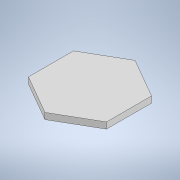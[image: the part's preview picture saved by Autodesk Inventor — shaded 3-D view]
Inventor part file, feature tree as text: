
AUTODESK INVENTOR PART (.ipt)
format: ipt  version: 2022.3 (Build 263350000, 350)  size: 94,208 bytes
history: native  units: in
note: dims shown in document units (in); Inventor stores cm internally (conversion verified against a paired STEP export)
features: extrude x1, sketch x1
ambient origin geometry x8: Origin, YZ Plane, XZ Plane, XY Plane, X Axis, Y Axis, Z Axis, Center Point
bodies: Solid1 (feature_tree)
feature tree (2):
  extrude  "Extrusion1"  Depth=0.1575in TaperAngle=0.0deg
  sketch  "Sketch1"  dims[d0=1.9685in d1=0.1575in d2=0.0in]
